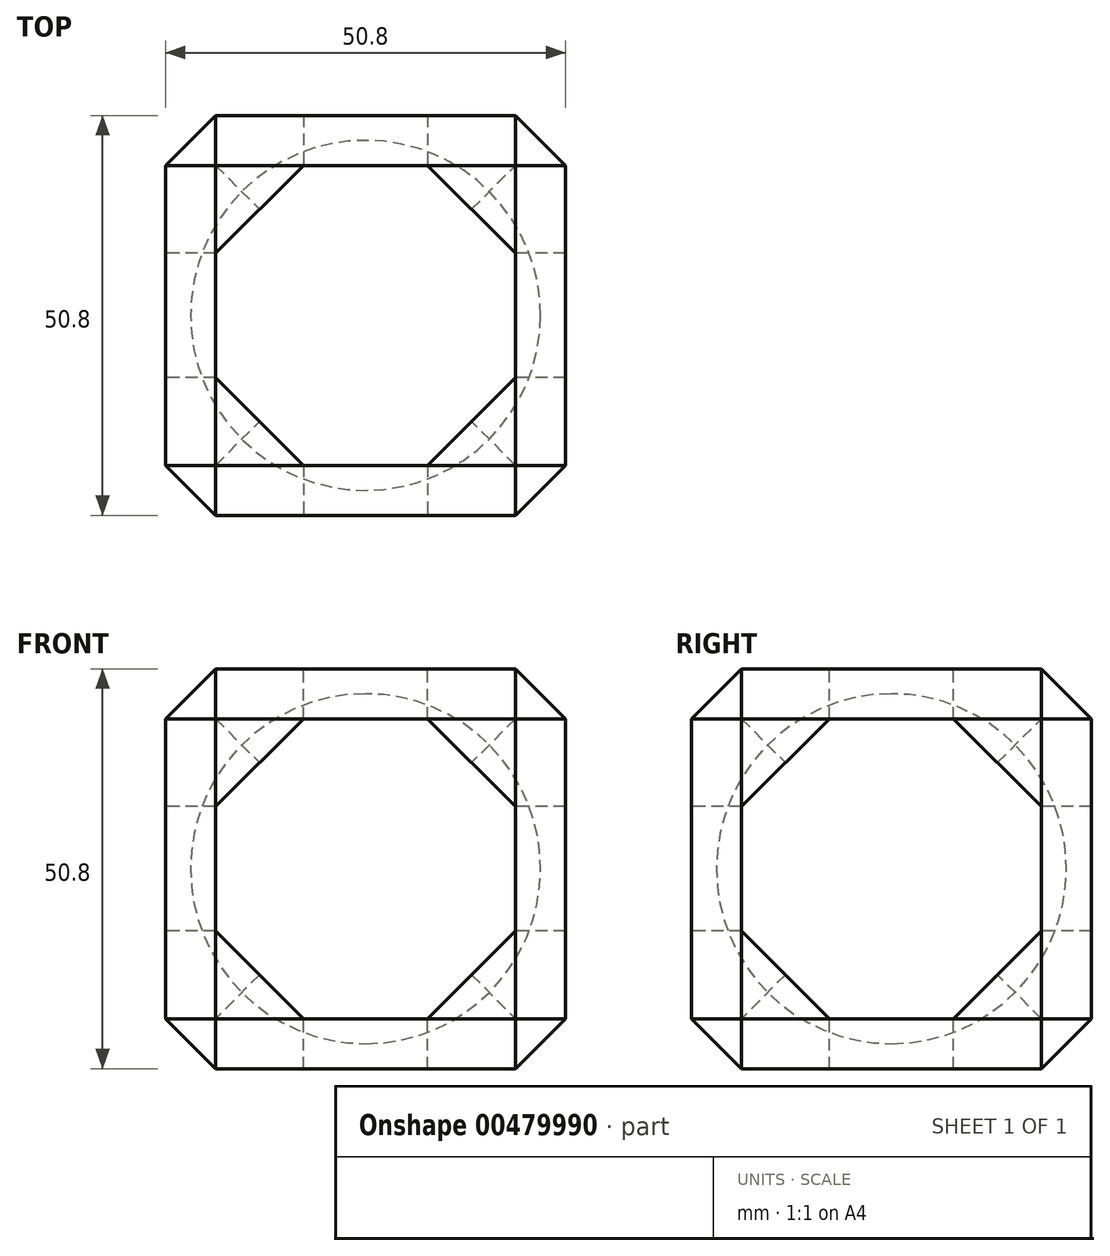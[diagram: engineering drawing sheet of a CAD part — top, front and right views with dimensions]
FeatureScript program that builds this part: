
annotation { "Feature Type Name" : "Feature", "Feature Type Description" : "" }
export const myFeature = defineFeature(function(context is Context, id is Id, definition is map)
    precondition{}
    {
        {
            var Q0;
            Q0=qCreatedBy(makeId("Top.planeOp"),FACE);
            var sketch = newSketch(context, id + "F0", { "sketchPlane" : qUnion([Q0])});
            skLineSegment(sketch, "E0.bottom", {"start": v(-25.4, -25.4) * mm, "end": v(25.4, -25.4) * mm});
            skLineSegment(sketch, "E0.top", {"start": v(-25.4, 25.4) * mm, "end": v(25.4, 25.4) * mm});
            skLineSegment(sketch, "E0.left", {"start": v(-25.4, -25.4) * mm, "end": v(-25.4, 25.4) * mm});
            skLineSegment(sketch, "E0.right", {"start": v(25.4, -25.4) * mm, "end": v(25.4, 25.4) * mm});
            skSolve(sketch);
        }
        {
            var Q0;
            Q0 = qSketchRegion(id + "F0", true);
            extrude(context, id + "F1", {"entities" : qUnion([Q0]), "depth" : 50.8 * mm});
        }
        {
            var Q0;
            Q0=makeQuery(id+"F1.opExtrude","CAP_FACE",FACE,{"disambiguationData":[OSD([sQuery(id+"F0.wireOp",EDGE,"E0.bottom"),sQuery(id+"F0.wireOp",EDGE,"E0.top"),sQuery(id+"F0.wireOp",EDGE,"E0.left"),sQuery(id+"F0.wireOp",EDGE,"E0.right")])],"isStart":false});
            var sketch = newSketch(context, id + "F2", { "sketchPlane" : qUnion([Q0])});
            skCircle(sketch, "E1.cCircle", {"center": v(0, 0) * mm, "radius": 19.05 * mm, "construction": true});
            skPoint(sketch, "E1.cCircle.perimeterSnap0", {"position": v(0, 25.4) * mm});
            skLineSegment(sketch, "E1.0", {"start": v(-7.9, 19.05) * mm, "end": v(7.9, 19.05) * mm});
            skLineSegment(sketch, "E1.1", {"start": v(7.9, 19.05) * mm, "end": v(19.05, 7.9) * mm});
            skLineSegment(sketch, "E1.2", {"start": v(19.05, 7.9) * mm, "end": v(19.05, -7.9) * mm});
            skLineSegment(sketch, "E1.3", {"start": v(19.05, -7.9) * mm, "end": v(7.9, -19.05) * mm});
            skLineSegment(sketch, "E1.4", {"start": v(7.9, -19.05) * mm, "end": v(-7.9, -19.05) * mm});
            skLineSegment(sketch, "E1.5", {"start": v(-7.9, -19.05) * mm, "end": v(-19.05, -7.9) * mm});
            skLineSegment(sketch, "E1.6", {"start": v(-19.05, -7.9) * mm, "end": v(-19.05, 7.9) * mm});
            skLineSegment(sketch, "E1.7", {"start": v(-19.05, 7.9) * mm, "end": v(-7.9, 19.05) * mm});
            skPoint(sketch, "E1.0.midPoint", {"position": v(0, 19.05) * mm});
            skPoint(sketch, "E1.0.midPoint.positionSnap0", {"position": v(0, 25.4) * mm});
            skSolve(sketch);
        }
        {
            var Q0;
            Q0 = qSketchRegion(id + "F2", true);
            extrude(context, id + "F3", {"entities" : qUnion([Q0]), "operationType" : NewBodyOperationType.REMOVE, "endBound" : BoundingType.THROUGH_ALL, "oppositeDirection" : true, "depth" : 25.4 * mm});
        }
        {
            var Q0;
            Q0=makeQuery(id+"F1.opExtrude","SWEPT_FACE",FACE,{"disambiguationData":[OSD([sQuery(id+"F0.wireOp",EDGE,"E0.left")])]});
            var sketch = newSketch(context, id + "F4", { "sketchPlane" : qUnion([Q0])});
            skCircle(sketch, "E2.cCircle", {"center": v(0, 25.4) * mm, "radius": 19.05 * mm, "construction": true});
            skLineSegment(sketch, "E2.0", {"start": v(7.9, 6.35) * mm, "end": v(-7.9, 6.35) * mm});
            skLineSegment(sketch, "E2.1", {"start": v(-7.9, 6.35) * mm, "end": v(-19.05, 17.5) * mm});
            skLineSegment(sketch, "E2.2", {"start": v(-19.05, 17.5) * mm, "end": v(-19.05, 33.3) * mm});
            skLineSegment(sketch, "E2.3", {"start": v(-19.05, 33.3) * mm, "end": v(-7.9, 44.45) * mm});
            skLineSegment(sketch, "E2.4", {"start": v(-7.9, 44.45) * mm, "end": v(7.9, 44.45) * mm});
            skLineSegment(sketch, "E2.5", {"start": v(7.9, 44.45) * mm, "end": v(19.05, 33.3) * mm});
            skLineSegment(sketch, "E2.6", {"start": v(19.05, 33.3) * mm, "end": v(19.05, 17.5) * mm});
            skLineSegment(sketch, "E2.7", {"start": v(19.05, 17.5) * mm, "end": v(7.9, 6.35) * mm});
            skPoint(sketch, "E2.0.midPoint", {"position": v(0, 6.35) * mm});
            skSolve(sketch);
        }
        {
            var Q0;
            Q0 = qSketchRegion(id + "F4", true);
            extrude(context, id + "F5", {"entities" : qUnion([Q0]), "operationType" : NewBodyOperationType.REMOVE, "endBound" : BoundingType.THROUGH_ALL, "oppositeDirection" : true, "depth" : 25.4 * mm});
        }
        {
            var Q0;
            Q0=makeQuery(id+"F1.opExtrude","SWEPT_FACE",FACE,{"disambiguationData":[OSD([sQuery(id+"F0.wireOp",EDGE,"E0.bottom")])]});
            var sketch = newSketch(context, id + "F6", { "sketchPlane" : qUnion([Q0])});
            skCircle(sketch, "E3.cCircle", {"center": v(0, 25.4) * mm, "radius": 19.05 * mm, "construction": true});
            skLineSegment(sketch, "E3.0", {"start": v(7.9, 6.35) * mm, "end": v(-7.9, 6.35) * mm});
            skLineSegment(sketch, "E3.1", {"start": v(-7.9, 6.35) * mm, "end": v(-19.05, 17.5) * mm});
            skLineSegment(sketch, "E3.2", {"start": v(-19.05, 17.5) * mm, "end": v(-19.05, 33.3) * mm});
            skLineSegment(sketch, "E3.3", {"start": v(-19.05, 33.3) * mm, "end": v(-7.9, 44.45) * mm});
            skLineSegment(sketch, "E3.4", {"start": v(-7.9, 44.45) * mm, "end": v(7.9, 44.45) * mm});
            skLineSegment(sketch, "E3.5", {"start": v(7.9, 44.45) * mm, "end": v(19.05, 33.3) * mm});
            skLineSegment(sketch, "E3.6", {"start": v(19.05, 33.3) * mm, "end": v(19.05, 17.5) * mm});
            skLineSegment(sketch, "E3.7", {"start": v(19.05, 17.5) * mm, "end": v(7.9, 6.35) * mm});
            skPoint(sketch, "E3.0.midPoint", {"position": v(0, 6.35) * mm});
            skSolve(sketch);
        }
        {
            var Q0;
            Q0 = qSketchRegion(id + "F6", true);
            extrude(context, id + "F7", {"entities" : qUnion([Q0]), "operationType" : NewBodyOperationType.REMOVE, "endBound" : BoundingType.THROUGH_ALL, "oppositeDirection" : true, "depth" : 25.4 * mm});
        }
        {
            var Q0;
            Q0=makeQuery(id+"F1.opExtrude","CAP_EDGE",EDGE,{"disambiguationData":[OSD([sQuery(id+"F0.wireOp",EDGE,"E0.right")])],"isStart":true});
            var Q1;
            Q1=makeQuery(id+"F1.opExtrude","CAP_EDGE",EDGE,{"disambiguationData":[OSD([sQuery(id+"F0.wireOp",EDGE,"E0.bottom")])],"isStart":true});
            var Q2;
            Q2=makeQuery(id+"F1.opExtrude","SWEPT_EDGE",EDGE,{"disambiguationData":[OSD([sQuery(id+"F0.wireOp",EDGE,"E0.bottom"),sQuery(id+"F0.wireOp",EDGE,"E0.right")])]});
            var Q3;
            Q3=makeQuery(id+"F1.opExtrude","SWEPT_EDGE",EDGE,{"disambiguationData":[OSD([sQuery(id+"F0.wireOp",EDGE,"E0.top"),sQuery(id+"F0.wireOp",EDGE,"E0.right")])]});
            var Q4;
            Q4=makeQuery(id+"F1.opExtrude","CAP_EDGE",EDGE,{"disambiguationData":[OSD([sQuery(id+"F0.wireOp",EDGE,"E0.right")])],"isStart":false});
            var Q5;
            Q5=makeQuery(id+"F1.opExtrude","CAP_EDGE",EDGE,{"disambiguationData":[OSD([sQuery(id+"F0.wireOp",EDGE,"E0.top")])],"isStart":false});
            var Q6;
            Q6=makeQuery(id+"F1.opExtrude","SWEPT_EDGE",EDGE,{"disambiguationData":[OSD([sQuery(id+"F0.wireOp",EDGE,"E0.top"),sQuery(id+"F0.wireOp",EDGE,"E0.left")])]});
            var Q7;
            Q7=makeQuery(id+"F1.opExtrude","CAP_EDGE",EDGE,{"disambiguationData":[OSD([sQuery(id+"F0.wireOp",EDGE,"E0.top")])],"isStart":true});
            var Q8;
            Q8=makeQuery(id+"F1.opExtrude","CAP_EDGE",EDGE,{"disambiguationData":[OSD([sQuery(id+"F0.wireOp",EDGE,"E0.left")])],"isStart":true});
            var Q9;
            Q9=makeQuery(id+"F1.opExtrude","SWEPT_EDGE",EDGE,{"disambiguationData":[OSD([sQuery(id+"F0.wireOp",EDGE,"E0.bottom"),sQuery(id+"F0.wireOp",EDGE,"E0.left")])]});
            var Q10;
            Q10=makeQuery(id+"F1.opExtrude","CAP_EDGE",EDGE,{"disambiguationData":[OSD([sQuery(id+"F0.wireOp",EDGE,"E0.left")])],"isStart":false});
            var Q11;
            Q11=makeQuery(id+"F1.opExtrude","CAP_EDGE",EDGE,{"disambiguationData":[OSD([sQuery(id+"F0.wireOp",EDGE,"E0.bottom")])],"isStart":false});
            chamfer(context, id + "F8", {"entities" : qUnion([Q0, Q1, Q2, Q3, Q4, Q5, Q6, Q7, Q8, Q9, Q10, Q11]), "width" : 6.35 * mm, "tangentPropagation" : true});
        }
        {
            var Q0;
            Q0=qCreatedBy(makeId("Front.planeOp"),FACE);
            var sketch = newSketch(context, id + "F9", { "sketchPlane" : qUnion([Q0])});
            skLineSegment(sketch, "E4", {"start": v(0, 47.62) * mm, "end": v(0, 3.18) * mm});
            skArc(sketch, "E5", {"start": v(0, 3.17) * mm, "mid": v(-22.22, 25.4) * mm, "end": v(0, 47.62) * mm});
            skSolve(sketch);
        }
        {
            var Q0;
            Q0=qCreatedBy(makeId("Front.planeOp"),FACE);
            var sketch = newSketch(context, id + "F10", { "sketchPlane" : qUnion([Q0])});
            skLineSegment(sketch, "E6", {"start": v(0, 0) * mm, "end": v(0, 55.68) * mm});
            skSolve(sketch);
        }
        {
            var Q0;
            Q0 = qSketchRegion(id + "F9", true);
            var Q1;
            Q1=sQuery(id+"F10.wireOp",EDGE,"E6");
            revolve(context, id + "F11", {"entities" : qUnion([Q0]), "axis" : qUnion([Q1]), "revolveType" : RevolveType.FULL});
        }
    });
